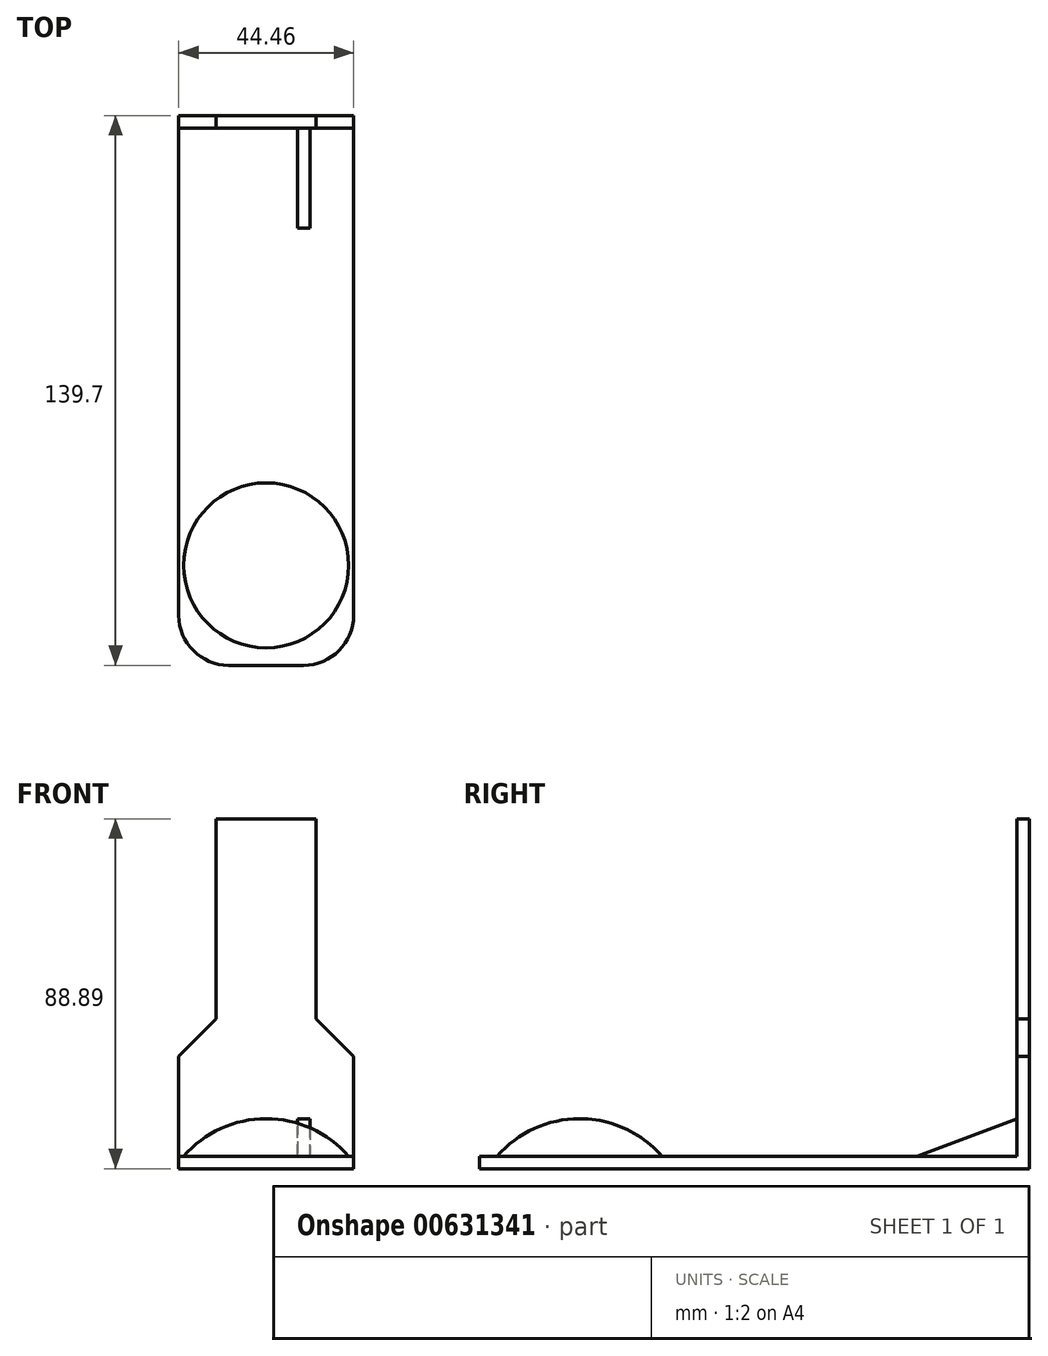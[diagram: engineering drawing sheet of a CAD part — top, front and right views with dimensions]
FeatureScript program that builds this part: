
annotation { "Feature Type Name" : "Feature", "Feature Type Description" : "" }
export const myFeature = defineFeature(function(context is Context, id is Id, definition is map)
    precondition{}
    {
        {
            var Q0;
            Q0=qCreatedBy(makeId("Right.planeOp"),FACE);
            var sketch = newSketch(context, id + "F0", { "sketchPlane" : qUnion([Q0])});
            skLineSegment(sketch, "E0", {"start": v(-25.4, 0) * mm, "end": v(-25.4, -3.17) * mm});
            skLineSegment(sketch, "E1", {"start": v(-25.4, -3.17) * mm, "end": v(114.3, -3.17) * mm});
            skLineSegment(sketch, "E2", {"start": v(114.3, -3.17) * mm, "end": v(114.3, 0) * mm});
            skLineSegment(sketch, "E3", {"start": v(114.3, 0) * mm, "end": v(-25.4, 0) * mm});
            skSolve(sketch);
        }
        {
            var Q0;
            Q0 = qSketchRegion(id + "F0", true);
            extrude(context, id + "F1", {"entities" : qUnion([Q0]), "endBound" : BoundingType.SYMMETRIC, "depth" : 44.45 * mm, "offsetDistance" : 25.4 * mm});
        }
        {
            var Q0;
            Q0=qCreatedBy(makeId("Right.planeOp"),FACE);
            var sketch = newSketch(context, id + "F2", { "sketchPlane" : qUnion([Q0])});
            skArc(sketch, "E4", {"start": v(0, 9.53) * mm, "mid": v(-11.5, 7.03) * mm, "end": v(-20.95, 0) * mm});
            skLineSegment(sketch, "E5", {"start": v(0, 9.53) * mm, "end": v(0, 0) * mm});
            skLineSegment(sketch, "E6", {"start": v(0, 0) * mm, "end": v(-20.96, 0) * mm});
            skSolve(sketch);
        }
        {
            var Q0;
            Q0 = qSketchRegion(id + "F2", true);
            var Q1;
            Q1=sQuery(id+"F2.wireOp",EDGE,"E5");
            revolve(context, id + "F3", {"operationType" : NewBodyOperationType.ADD, "entities" : qUnion([Q0]), "axis" : qUnion([Q1]), "revolveType" : RevolveType.FULL});
        }
        {
            var Q0;
            Q0=makeQuery(id+"F1.opExtrude","CAP_EDGE",EDGE,{"disambiguationData":[OSD([sQuery(id+"F0.wireOp",EDGE,"E0")])],"isStart":false});
            var Q1;
            Q1=makeQuery(id+"F1.opExtrude","CAP_EDGE",EDGE,{"disambiguationData":[OSD([sQuery(id+"F0.wireOp",EDGE,"E0")])],"isStart":true});
            fillet(context, id + "F4", {"entities" : qUnion([Q0, Q1]), "radius" : 12.7 * mm, "tangentPropagation" : true, "allowEdgeOverflow" : false});
        }
        {
            var Q0;
            Q0=makeQuery(id+"F1.opExtrude","SWEPT_FACE",FACE,{"disambiguationData":[OSD([sQuery(id+"F0.wireOp",EDGE,"E2")])]});
            var sketch = newSketch(context, id + "F5", { "sketchPlane" : qUnion([Q0])});
            skLineSegment(sketch, "E7", {"start": v(-22.23, 0) * mm, "end": v(-22.23, 25.4) * mm});
            skLineSegment(sketch, "E8", {"start": v(-22.23, 25.4) * mm, "end": v(-12.7, 34.93) * mm});
            skLineSegment(sketch, "E9", {"start": v(-12.7, 34.93) * mm, "end": v(-12.7, 85.73) * mm});
            skLineSegment(sketch, "E10", {"start": v(22.23, 0) * mm, "end": v(22.23, 25.4) * mm});
            skLineSegment(sketch, "E11", {"start": v(22.23, 25.4) * mm, "end": v(12.7, 34.93) * mm});
            skLineSegment(sketch, "E12", {"start": v(12.7, 34.93) * mm, "end": v(12.7, 85.73) * mm});
            skLineSegment(sketch, "E13", {"start": v(12.7, 85.73) * mm, "end": v(-12.7, 85.73) * mm});
            skLineSegment(sketch, "E14", {"start": v(-22.23, 0) * mm, "end": v(22.23, 0) * mm});
            skSolve(sketch);
        }
        {
            var Q0;
            Q0 = qSketchRegion(id + "F5", true);
            extrude(context, id + "F6", {"entities" : qUnion([Q0]), "operationType" : NewBodyOperationType.ADD, "oppositeDirection" : true, "depth" : 3.17 * mm, "offsetDistance" : 25.4 * mm});
        }
        {
            var Q0;
            Q0=qCreatedBy(makeId("Right.planeOp"),FACE);
            cPlane(context, id + "F7", {"entities" : qUnion([Q0]), "cplaneType" : CPlaneType.OFFSET, "offset" : 9.52 * mm, "width" : 152.4 * mm, "height" : 152.4 * mm});
        }
        {
            var Q0;
            Q0=qCreatedBy(id+"F7.planeOp",FACE);
            var sketch = newSketch(context, id + "F8", { "sketchPlane" : qUnion([Q0])});
            skLineSegment(sketch, "E15", {"start": v(111.13, 9.53) * mm, "end": v(85.73, 0) * mm});
            skLineSegment(sketch, "E16", {"start": v(85.73, 0) * mm, "end": v(111.13, 0) * mm});
            skLineSegment(sketch, "E17", {"start": v(111.13, 0) * mm, "end": v(111.13, 9.53) * mm});
            skSolve(sketch);
        }
        {
            var Q0;
            Q0 = qSketchRegion(id + "F8", true);
            extrude(context, id + "F9", {"entities" : qUnion([Q0]), "operationType" : NewBodyOperationType.ADD, "endBound" : BoundingType.SYMMETRIC, "depth" : 3.17 * mm, "offsetDistance" : 25.4 * mm});
        }
    });
